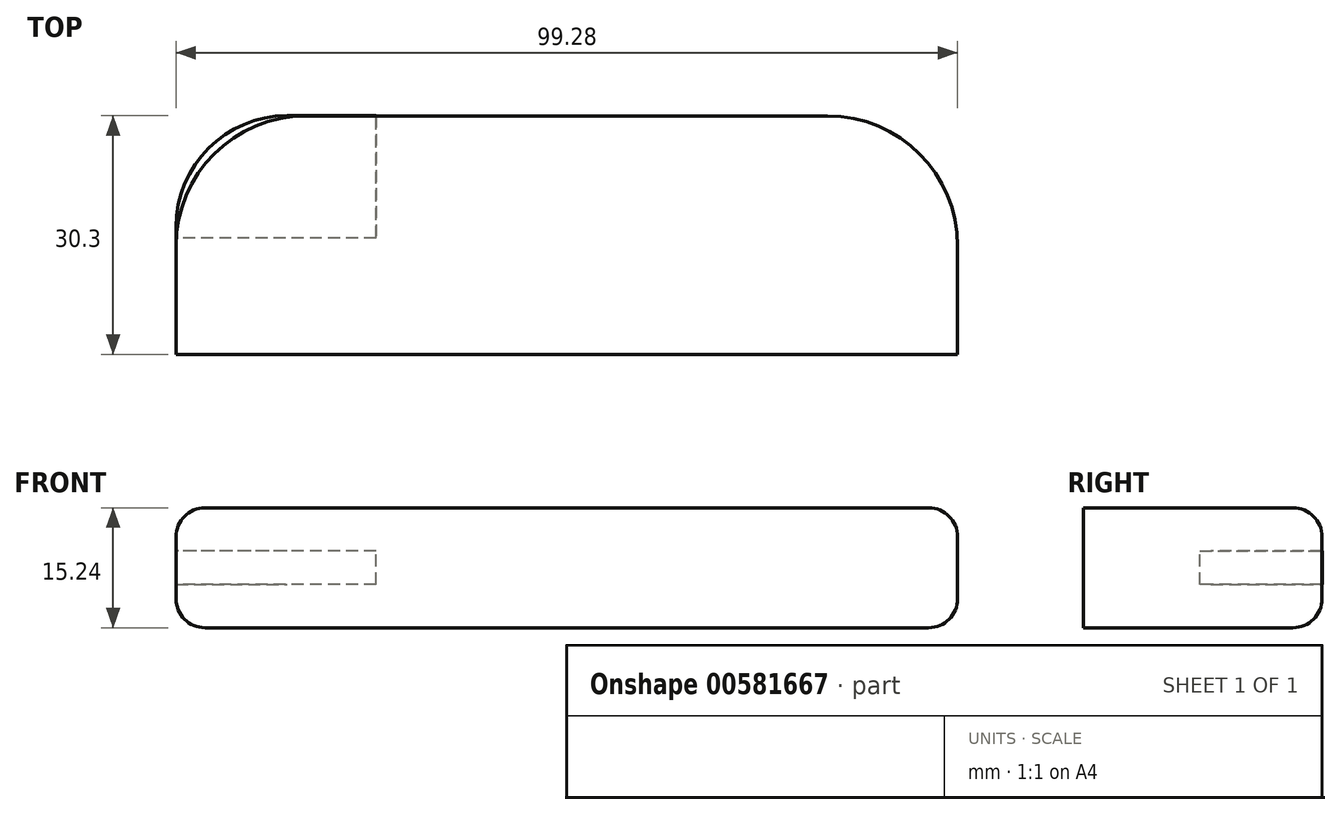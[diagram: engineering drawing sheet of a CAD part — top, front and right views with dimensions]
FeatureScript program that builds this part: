
annotation { "Feature Type Name" : "Feature", "Feature Type Description" : "" }
export const myFeature = defineFeature(function(context is Context, id is Id, definition is map)
    precondition{}
    {
        {
            var Q0;
            Q0=qCreatedBy(makeId("Top.planeOp"),FACE);
            var sketch = newSketch(context, id + "F0", { "sketchPlane" : qUnion([Q0])});
            skLineSegment(sketch, "E0.bottom", {"start": v(-29.95, -18.44) * mm, "end": v(36.3, -18.44) * mm});
            skLineSegment(sketch, "E0.top", {"start": v(-46.46, -48.71) * mm, "end": v(52.82, -48.71) * mm});
            skLineSegment(sketch, "E0.left", {"start": v(-46.46, -34.95) * mm, "end": v(-46.46, -48.71) * mm});
            skLineSegment(sketch, "E0.right", {"start": v(52.82, -34.95) * mm, "end": v(52.82, -48.71) * mm});
            skPoint(sketch, "E1.visualSharp", {"position": v(52.82, -18.44) * mm});
            skArc(sketch, "E1.filletArc", {"start": v(52.82, -34.95) * mm, "mid": v(47.98, -23.27) * mm, "end": v(36.3, -18.44) * mm});
            skPoint(sketch, "E2.visualSharp", {"position": v(-46.46, -18.44) * mm});
            skArc(sketch, "E2.filletArc", {"start": v(-29.95, -18.44) * mm, "mid": v(-41.62, -23.27) * mm, "end": v(-46.46, -34.95) * mm});
            skSolve(sketch);
        }
        {
            var Q0;
            Q0 = qSketchRegion(id + "F0", true);
            extrude(context, id + "F1", {"entities" : qUnion([Q0]), "depth" : 15.24 * mm, "offsetDistance" : 25.4 * mm});
        }
        {
            var Q0;
            Q0=makeQuery(id+"F1.opExtrude","CAP_EDGE",EDGE,{"disambiguationData":[OSD([sQuery(id+"F0.wireOp",EDGE,"E0.bottom")])],"isStart":false});
            var Q1;
            Q1=makeQuery(id+"F1.opExtrude","CAP_EDGE",EDGE,{"disambiguationData":[OSD([sQuery(id+"F0.wireOp",EDGE,"E0.bottom")])],"isStart":true});
            fillet(context, id + "F2", {"entities" : qUnion([Q0, Q1]), "radius" : 3.68 * mm, "tangentPropagation" : true, "allowEdgeOverflow" : false});
        }
        {
            var Q0;
            Q0=makeQuery(id+"F1.opExtrude","SWEPT_FACE",FACE,{"disambiguationData":[OSD([sQuery(id+"F0.wireOp",EDGE,"E0.left")])]});
            var sketch = newSketch(context, id + "F3", { "sketchPlane" : qUnion([Q0])});
            skLineSegment(sketch, "E3", {"start": v(33.93, 9.75) * mm, "end": v(18.4, 9.75) * mm});
            skLineSegment(sketch, "E4", {"start": v(18.4, 9.75) * mm, "end": v(18.4, 5.52) * mm});
            skLineSegment(sketch, "E5", {"start": v(18.4, 5.52) * mm, "end": v(33.93, 5.52) * mm});
            skLineSegment(sketch, "E6", {"start": v(33.93, 5.52) * mm, "end": v(33.93, 9.75) * mm});
            skSolve(sketch);
        }
        {
            var Q0;
            Q0 = qSketchRegion(id + "F3", true);
            extrude(context, id + "F4", {"entities" : qUnion([Q0]), "oppositeDirection" : true, "depth" : 25.4 * mm, "offsetDistance" : 25.4 * mm});
        }
        {
            var Q0;
            Q0=makeQuery(id+"F4.opExtrude","CAP_EDGE",EDGE,{"disambiguationData":[OSD([sQuery(id+"F3.wireOp",EDGE,"E4")])],"isStart":true});
            fillet(context, id + "F5", {"entities" : qUnion([Q0]), "radius" : 14.1 * mm, "tangentPropagation" : true, "allowEdgeOverflow" : false});
        }
    });
